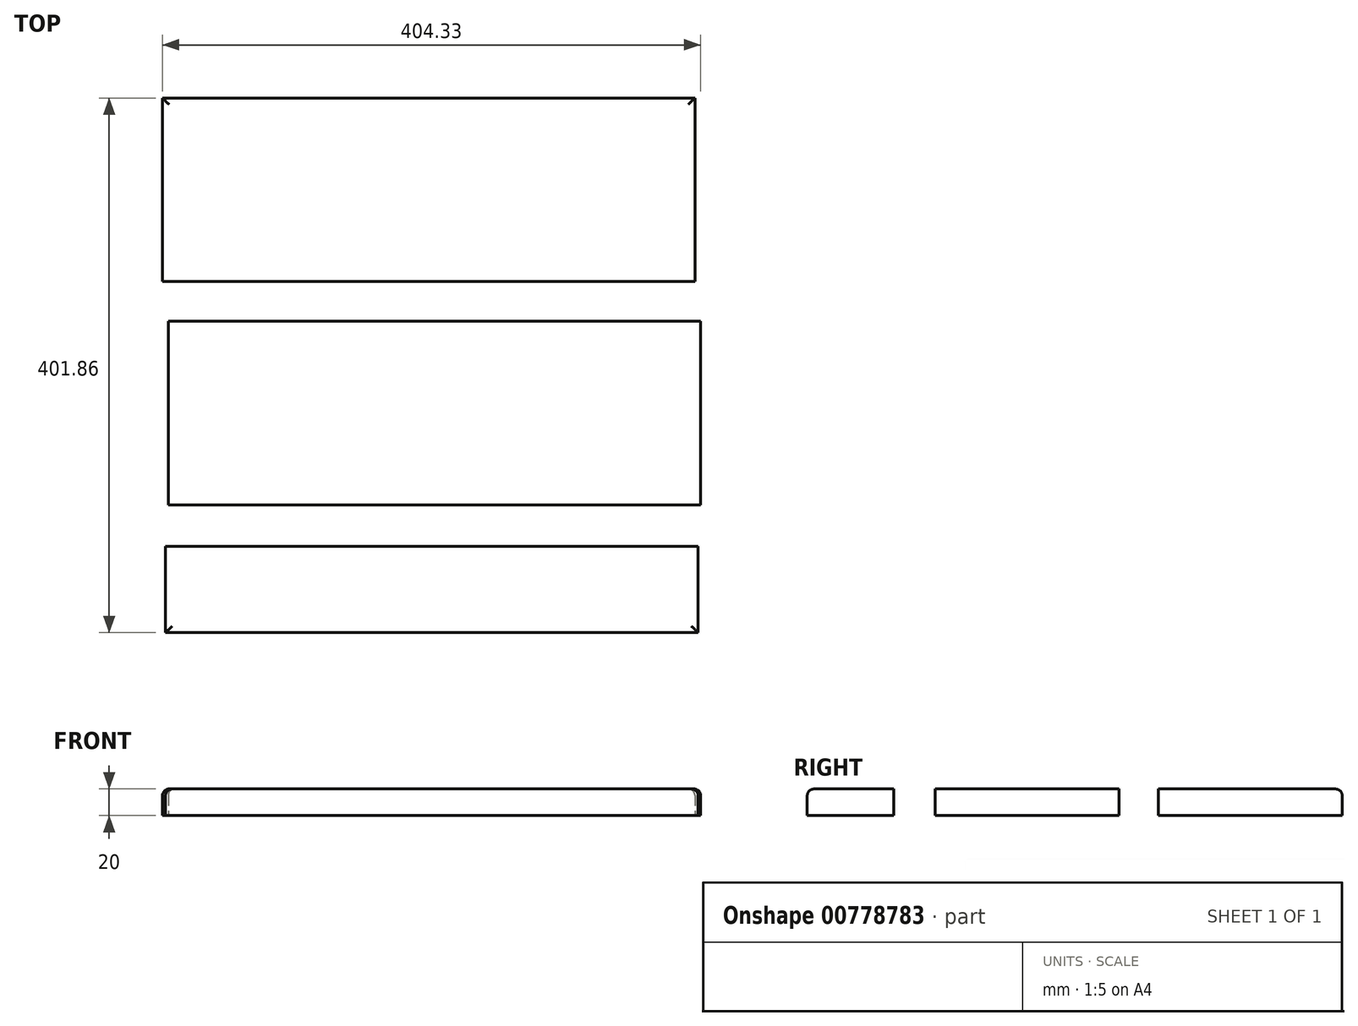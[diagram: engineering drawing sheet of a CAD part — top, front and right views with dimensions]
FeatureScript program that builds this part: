
annotation { "Feature Type Name" : "Feature", "Feature Type Description" : "" }
export const myFeature = defineFeature(function(context is Context, id is Id, definition is map)
    precondition{}
    {
        {
            var Q0;
            Q0=qCreatedBy(makeId("Top.planeOp"),FACE);
            var sketch = newSketch(context, id + "F0", { "sketchPlane" : qUnion([Q0])});
            skLineSegment(sketch, "E0.bottom", {"start": v(-400, 138) * mm, "end": v(0, 138) * mm});
            skLineSegment(sketch, "E0.top", {"start": v(-400, 0) * mm, "end": v(0, 0) * mm});
            skLineSegment(sketch, "E0.left", {"start": v(-400, 138) * mm, "end": v(-400, 0) * mm});
            skLineSegment(sketch, "E0.right", {"start": v(0, 138) * mm, "end": v(0, 0) * mm});
            skLineSegment(sketch, "E1.bottom", {"start": v(-395.67, -29.76) * mm, "end": v(4.33, -29.76) * mm});
            skLineSegment(sketch, "E1.top", {"start": v(-395.67, -167.76) * mm, "end": v(4.33, -167.76) * mm});
            skLineSegment(sketch, "E1.left", {"start": v(-395.67, -29.76) * mm, "end": v(-395.67, -167.76) * mm});
            skLineSegment(sketch, "E1.right", {"start": v(4.33, -29.76) * mm, "end": v(4.33, -167.76) * mm});
            skLineSegment(sketch, "E2.bottom", {"start": v(-397.66, -198.86) * mm, "end": v(2.34, -198.86) * mm});
            skLineSegment(sketch, "E2.top", {"start": v(-397.66, -263.86) * mm, "end": v(2.34, -263.86) * mm});
            skLineSegment(sketch, "E2.left", {"start": v(-397.66, -198.86) * mm, "end": v(-397.66, -263.86) * mm});
            skLineSegment(sketch, "E2.right", {"start": v(2.34, -198.86) * mm, "end": v(2.34, -263.86) * mm});
            skSolve(sketch);
        }
        {
            var Q0;
            Q0=makeQuery(id+"F0.imprint","IMPRINT",FACE,{"disambiguationData":[TD([[makeQuery(id+"F0.imprint","IMPRINT",EDGE,{"derivedFrom":sQuery(id+"F0.wireOp",EDGE,"E0.bottom")}),-1.0]])]});
            var Q1;
            Q1=makeQuery(id+"F0.imprint","IMPRINT",FACE,{"disambiguationData":[TD([[makeQuery(id+"F0.imprint","IMPRINT",EDGE,{"derivedFrom":sQuery(id+"F0.wireOp",EDGE,"E1.bottom")}),-1.0]])]});
            var Q2;
            Q2=makeQuery(id+"F0.imprint","IMPRINT",FACE,{"disambiguationData":[TD([[makeQuery(id+"F0.imprint","IMPRINT",EDGE,{"derivedFrom":sQuery(id+"F0.wireOp",EDGE,"E2.bottom")}),-1.0]])]});
            extrude(context, id + "F1", {"entities" : qUnion([Q0, Q1, Q2]), "depth" : 20 * mm, "offsetDistance" : 25 * mm});
        }
        {
            var Q0;
            Q0=makeQuery(id+"F1.opExtrude","CAP_EDGE",EDGE,{"disambiguationData":[OSD([sQuery(id+"F0.wireOp",EDGE,"E2.left")])],"isStart":false});
            var Q1;
            Q1=makeQuery(id+"F1.opExtrude","CAP_EDGE",EDGE,{"disambiguationData":[OSD([sQuery(id+"F0.wireOp",EDGE,"E2.right")])],"isStart":false});
            var Q2;
            Q2=makeQuery(id+"F1.opExtrude","CAP_EDGE",EDGE,{"disambiguationData":[OSD([sQuery(id+"F0.wireOp",EDGE,"E2.top")])],"isStart":false});
            var Q3;
            Q3=makeQuery(id+"F1.opExtrude","CAP_EDGE",EDGE,{"disambiguationData":[OSD([sQuery(id+"F0.wireOp",EDGE,"E1.left")])],"isStart":false});
            var Q4;
            Q4=makeQuery(id+"F1.opExtrude","CAP_EDGE",EDGE,{"disambiguationData":[OSD([sQuery(id+"F0.wireOp",EDGE,"E1.right")])],"isStart":false});
            var Q5;
            Q5=makeQuery(id+"F1.opExtrude","CAP_EDGE",EDGE,{"disambiguationData":[OSD([sQuery(id+"F0.wireOp",EDGE,"E0.right")])],"isStart":false});
            var Q6;
            Q6=makeQuery(id+"F1.opExtrude","CAP_EDGE",EDGE,{"disambiguationData":[OSD([sQuery(id+"F0.wireOp",EDGE,"E0.left")])],"isStart":false});
            var Q7;
            Q7=makeQuery(id+"F1.opExtrude","CAP_EDGE",EDGE,{"disambiguationData":[OSD([sQuery(id+"F0.wireOp",EDGE,"E0.bottom")])],"isStart":false});
            fillet(context, id + "F2", {"entities" : qUnion([Q0, Q1, Q2, Q3, Q4, Q5, Q6, Q7]), "radius" : 5 * mm, "tangentPropagation" : true, "allowEdgeOverflow" : false});
        }
    });
